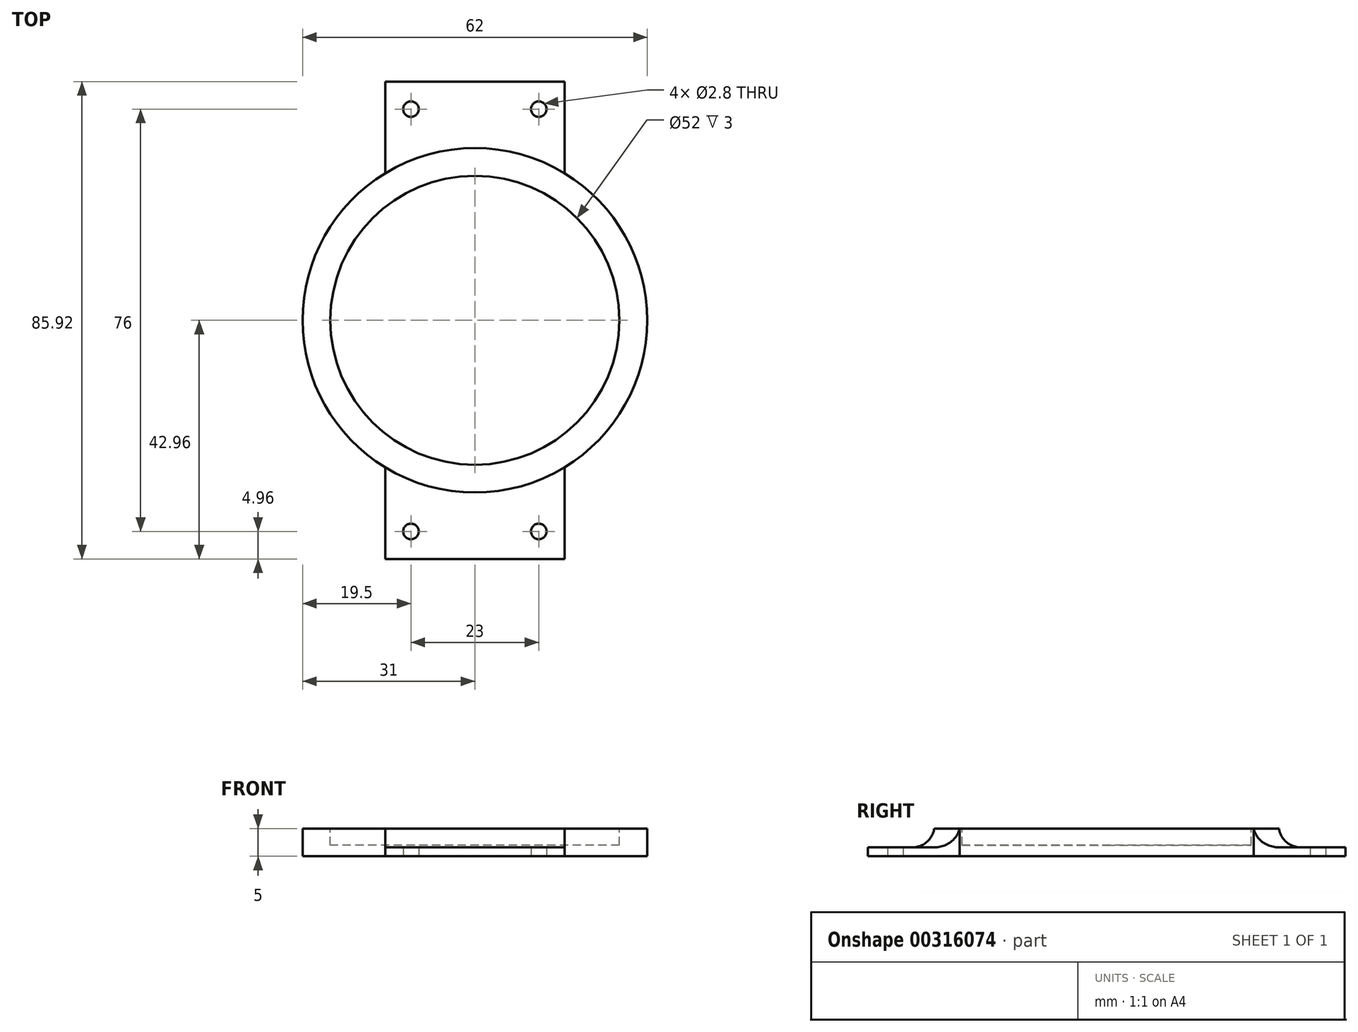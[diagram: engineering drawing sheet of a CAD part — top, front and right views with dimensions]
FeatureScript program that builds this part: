
annotation { "Feature Type Name" : "Feature", "Feature Type Description" : "" }
export const myFeature = defineFeature(function(context is Context, id is Id, definition is map)
    precondition{}
    {
        {
            var Q0;
            Q0=qCreatedBy(makeId("Top.planeOp"),FACE);
            var sketch = newSketch(context, id + "F0", { "sketchPlane" : qUnion([Q0])});
            skCircle(sketch, "E0", {"center": v(-11.5, 0) * mm, "radius": 1.4 * mm});
            skCircle(sketch, "E1", {"center": v(11.5, 0) * mm, "radius": 1.4 * mm});
            skLineSegment(sketch, "E2", {"start": v(-11.5, 0) * mm, "end": v(11.5, 0) * mm, "construction": true});
            skPoint(sketch, "E3", {"position": v(0, 0) * mm});
            skLineSegment(sketch, "E4.bottom", {"start": v(-16.14, -4.96) * mm, "end": v(16.14, -4.96) * mm});
            skLineSegment(sketch, "E4.top", {"start": v(-16.14, 4.96) * mm, "end": v(16.14, 4.96) * mm});
            skLineSegment(sketch, "E4.left", {"start": v(-16.14, -4.96) * mm, "end": v(-16.14, 4.96) * mm});
            skLineSegment(sketch, "E4.right", {"start": v(16.14, -4.96) * mm, "end": v(16.14, 4.96) * mm});
            skLineSegment(sketch, "E5", {"start": v(-11.5, 0) * mm, "end": v(-16.14, 0) * mm, "construction": true});
            skLineSegment(sketch, "E6", {"start": v(11.5, 0) * mm, "end": v(16.14, 0) * mm, "construction": true});
            skLineSegment(sketch, "E7", {"start": v(-11.5, 0) * mm, "end": v(-11.5, -4.96) * mm, "construction": true});
            skLineSegment(sketch, "E8", {"start": v(-11.5, 0) * mm, "end": v(-11.5, 4.96) * mm, "construction": true});
            skCircle(sketch, "E9", {"center": v(0, -38) * mm, "radius": 26 * mm});
            skCircle(sketch, "E10", {"center": v(0, -38) * mm, "radius": 31 * mm});
            skSolve(sketch);
        }
        {
            var Q0;
            Q0=makeQuery(id+"F0.imprint","IMPRINT",FACE,{"disambiguationData":[TD([[makeQuery(id+"F0.imprint","IMPRINT",EDGE,{"derivedFrom":sQuery(id+"F0.wireOp",EDGE,"E0")}),-1.0]])]});
            extrude(context, id + "F1", {"entities" : qUnion([Q0]), "depth" : 1.6 * mm});
        }
        {
            var Q0;
            Q0=makeQuery(id+"F0.imprint","IMPRINT",FACE,{"disambiguationData":[TD([[makeQuery(id+"F0.imprint","IMPRINT",EDGE,{"derivedFrom":sQuery(id+"F0.wireOp",EDGE,"E9")}),-1.0]])]});
            var Q1;
            Q1=makeQuery(id+"F0.imprint","IMPRINT",FACE,{"disambiguationData":[TD([[makeQuery(id+"F0.imprint","IMPRINT",EDGE,{"derivedFrom":sQuery(id+"F0.wireOp",EDGE,"E9")}),1.0]])]});
            extrude(context, id + "F2", {"entities" : qUnion([Q0, Q1]), "depth" : 5 * mm});
        }
        {
            var Q0;
            Q0=makeQuery(id+"F1.opExtrude","SWEPT_FACE",FACE,{"disambiguationData":[OSD([sQuery(id+"F0.wireOp",EDGE,"E4.bottom")])]});
            extrude(context, id + "F3", {"entities" : qUnion([Q0]), "operationType" : NewBodyOperationType.ADD, "depth" : 9.4 * mm});
        }
        {
            var Q0;
            {var subQ0=sQuery(id+"F0.wireOp",EDGE,"E4.bottom");Q0=makeQuery(id+"F3.boolean.opBoolean","INTERSECT",EDGE,{"derivedFrom":[makeQuery(id+"F2.opExtrude","SWEPT_FACE",FACE,{"disambiguationData":[OSD([sQuery(id+"F0.wireOp",EDGE,"E10")])]}),makeQuery(id+"F3.opExtrude","SWEPT_FACE",FACE,{"disambiguationData":[OSD([subQ0]),TDD([makeQuery(id+"F1.opExtrude","CAP_EDGE",EDGE,{"disambiguationData":[OSD([subQ0])],"isStart":false})])]})]});}
            var Q1;
            {var subQ0=sQuery(id+"F0.wireOp",EDGE,"E4.bottom");Q1=makeQuery(id+"F3.boolean.opBoolean","INTERSECT",EDGE,{"derivedFrom":[makeQuery(id+"F2.opExtrude","SWEPT_FACE",FACE,{"disambiguationData":[OSD([sQuery(id+"F0.wireOp",EDGE,"E10")])]}),makeQuery(id+"F3.opExtrude","SWEPT_FACE",FACE,{"disambiguationData":[OSD([subQ0]),TDD([makeQuery(id+"F1.opExtrude","CAP_EDGE",EDGE,{"disambiguationData":[OSD([subQ0])],"isStart":true})])]})]});}
            fillet(context, id + "F4", {"entities" : qUnion([Q0, Q1]), "radius" : 4 * mm, "tangentPropagation" : true, "allowEdgeOverflow" : false});
        }
        {
            var Q0;
            Q0=makeQuery(id+"F2.opExtrude","CAP_FACE",FACE,{"disambiguationData":[OSD([sQuery(id+"F0.wireOp",EDGE,"E10")])],"isStart":false});
            var sketch = newSketch(context, id + "F5", { "sketchPlane" : qUnion([Q0])});
            skCircle(sketch, "E11", {"center": v(0, -38) * mm, "radius": 26 * mm});
            skSolve(sketch);
        }
        {
            var Q0;
            Q0=makeQuery(id+"F5.imprint","IMPRINT",FACE,{"disambiguationData":[TD([[makeQuery(id+"F5.imprint","IMPRINT",EDGE,{"derivedFrom":sQuery(id+"F5.wireOp",EDGE,"E11")}),1.0]])]});
            extrude(context, id + "F6", {"entities" : qUnion([Q0]), "operationType" : NewBodyOperationType.REMOVE, "oppositeDirection" : true, "depth" : 3 * mm});
        }
        {
            var Q0;
            Q0=sQuery(id+"F0.wireOp",VERTEX,"E10.center");
            var Q1;
            Q1=sQuery(id+"F0.wireOp",EDGE,"E9");
            cPlane(context, id + "F7", {"entities" : qUnion([Q0, Q1]), "cplaneType" : CPlaneType.CURVE_POINT, "offset" : 38.3 * mm, "width" : 150 * mm, "height" : 150 * mm});
        }
        {
            var Q0;
            Q0=makeQuery(id+"F1.opExtrude","SWEPT_BODY",BODY,{"disambiguationData":[OSD([sQuery(id+"F0.wireOp",EDGE,"E0"),sQuery(id+"F0.wireOp",EDGE,"E1"),sQuery(id+"F0.wireOp",EDGE,"E4.bottom"),sQuery(id+"F0.wireOp",EDGE,"E4.top"),sQuery(id+"F0.wireOp",EDGE,"E4.left"),sQuery(id+"F0.wireOp",EDGE,"E4.right")])]});
            var Q1;
            Q1=qCreatedBy(id+"F7.planeOp",FACE);
            mirror(context, id + "F8", {"operationType" : NewBodyOperationType.ADD, "entities" : qUnion([Q0]), "mirrorPlane" : qUnion([Q1])});
        }
    });
